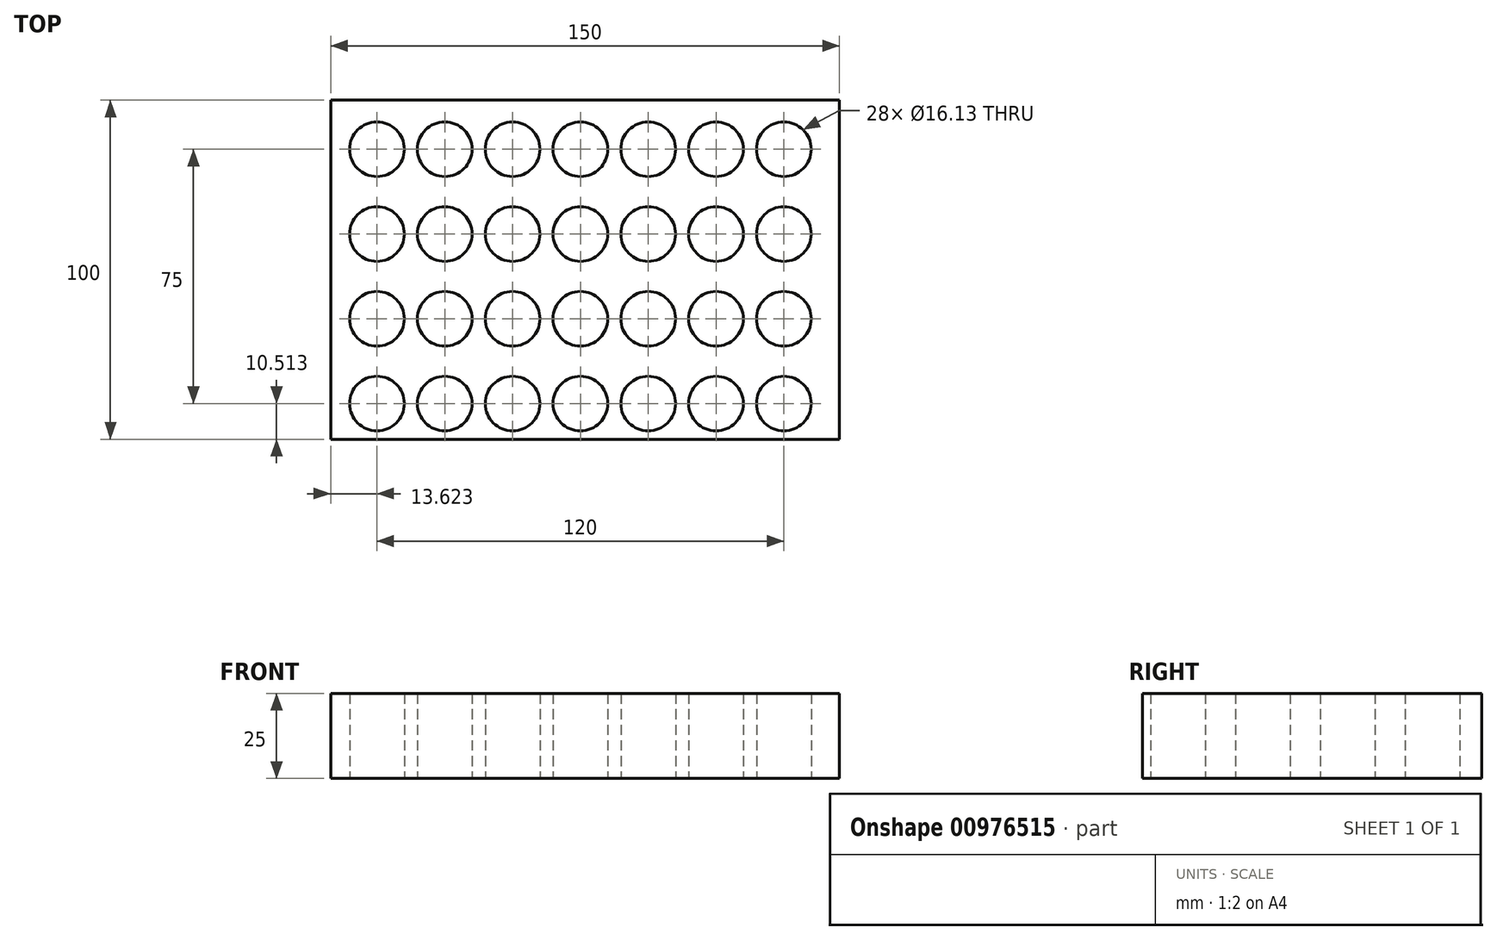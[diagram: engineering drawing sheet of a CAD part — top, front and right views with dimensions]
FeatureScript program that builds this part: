
annotation { "Feature Type Name" : "Feature", "Feature Type Description" : "" }
export const myFeature = defineFeature(function(context is Context, id is Id, definition is map)
    precondition{}
    {
        {
            var Q0;
            Q0=qCreatedBy(makeId("Top.planeOp"),FACE);
            var sketch = newSketch(context, id + "F0", { "sketchPlane" : qUnion([Q0])});
            skLineSegment(sketch, "E0.bottom", {"start": v(-75.35, 57.36) * mm, "end": v(74.65, 57.36) * mm});
            skLineSegment(sketch, "E0.top", {"start": v(-75.35, -42.64) * mm, "end": v(74.65, -42.64) * mm});
            skLineSegment(sketch, "E0.left", {"start": v(-75.35, 57.36) * mm, "end": v(-75.35, -42.64) * mm});
            skLineSegment(sketch, "E0.right", {"start": v(74.65, 57.36) * mm, "end": v(74.65, -42.64) * mm});
            skCircle(sketch, "E1", {"center": v(-61.73, 42.87) * mm, "radius": 8.06 * mm});
            skCircle(sketch, "E2.0.1.0", {"center": v(-61.73, 17.87) * mm, "radius": 8.06 * mm});
            skCircle(sketch, "E2.0.2.0", {"center": v(-61.73, -7.13) * mm, "radius": 8.06 * mm});
            skCircle(sketch, "E2.0.3.0", {"center": v(-61.73, -32.13) * mm, "radius": 8.06 * mm});
            skCircle(sketch, "E2.1.0.0", {"center": v(-41.73, 42.87) * mm, "radius": 8.06 * mm});
            skCircle(sketch, "E2.1.1.0", {"center": v(-41.73, 17.87) * mm, "radius": 8.06 * mm});
            skCircle(sketch, "E2.1.2.0", {"center": v(-41.73, -7.13) * mm, "radius": 8.06 * mm});
            skCircle(sketch, "E2.1.3.0", {"center": v(-41.73, -32.13) * mm, "radius": 8.06 * mm});
            skCircle(sketch, "E2.2.0.0", {"center": v(-21.73, 42.87) * mm, "radius": 8.06 * mm});
            skCircle(sketch, "E2.2.1.0", {"center": v(-21.73, 17.87) * mm, "radius": 8.06 * mm});
            skCircle(sketch, "E2.2.2.0", {"center": v(-21.73, -7.13) * mm, "radius": 8.06 * mm});
            skCircle(sketch, "E2.2.3.0", {"center": v(-21.73, -32.13) * mm, "radius": 8.06 * mm});
            skCircle(sketch, "E2.3.0.0", {"center": v(-1.73, 42.87) * mm, "radius": 8.06 * mm});
            skCircle(sketch, "E2.3.1.0", {"center": v(-1.73, 17.87) * mm, "radius": 8.06 * mm});
            skCircle(sketch, "E2.3.2.0", {"center": v(-1.73, -7.13) * mm, "radius": 8.06 * mm});
            skCircle(sketch, "E2.3.3.0", {"center": v(-1.73, -32.13) * mm, "radius": 8.06 * mm});
            skCircle(sketch, "E2.4.0.0", {"center": v(18.27, 42.87) * mm, "radius": 8.06 * mm});
            skCircle(sketch, "E2.4.1.0", {"center": v(18.27, 17.87) * mm, "radius": 8.06 * mm});
            skCircle(sketch, "E2.4.2.0", {"center": v(18.27, -7.13) * mm, "radius": 8.06 * mm});
            skCircle(sketch, "E2.4.3.0", {"center": v(18.27, -32.13) * mm, "radius": 8.06 * mm});
            skCircle(sketch, "E2.5.0.0", {"center": v(38.27, 42.87) * mm, "radius": 8.06 * mm});
            skCircle(sketch, "E2.5.1.0", {"center": v(38.27, 17.87) * mm, "radius": 8.06 * mm});
            skCircle(sketch, "E2.5.2.0", {"center": v(38.27, -7.13) * mm, "radius": 8.06 * mm});
            skCircle(sketch, "E2.5.3.0", {"center": v(38.27, -32.13) * mm, "radius": 8.06 * mm});
            skCircle(sketch, "E2.6.0.0", {"center": v(58.27, 42.87) * mm, "radius": 8.06 * mm});
            skCircle(sketch, "E2.6.1.0", {"center": v(58.27, 17.87) * mm, "radius": 8.06 * mm});
            skCircle(sketch, "E2.6.2.0", {"center": v(58.27, -7.13) * mm, "radius": 8.06 * mm});
            skCircle(sketch, "E2.6.3.0", {"center": v(58.27, -32.13) * mm, "radius": 8.06 * mm});
            skLineSegment(sketch, "E2.direction1", {"start": v(-61.73, 42.87) * mm, "end": v(-41.73, 42.87) * mm, "construction": true});
            skLineSegment(sketch, "E2.direction2", {"start": v(-61.73, 42.87) * mm, "end": v(-61.73, 17.87) * mm, "construction": true});
            skSolve(sketch);
        }
        {
            var Q0;
            Q0 = qSketchRegion(id + "F0", true);
            extrude(context, id + "F1", {"entities" : qUnion([Q0]), "depth" : 25 * mm, "offsetDistance" : 25 * mm});
        }
    });
